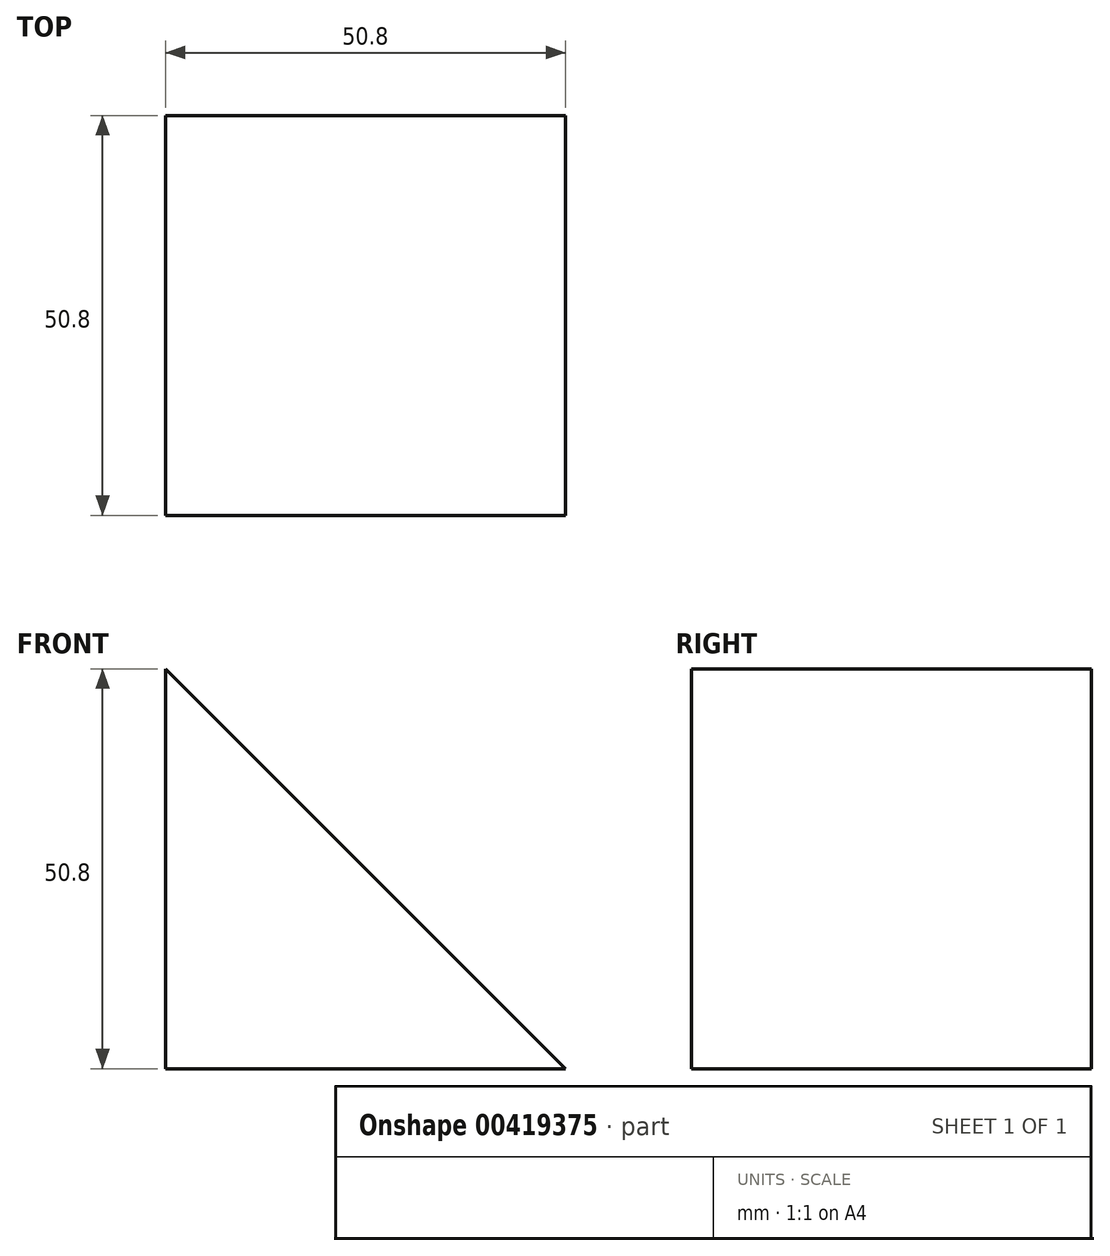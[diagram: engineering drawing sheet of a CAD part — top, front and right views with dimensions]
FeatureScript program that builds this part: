
annotation { "Feature Type Name" : "Feature", "Feature Type Description" : "" }
export const myFeature = defineFeature(function(context is Context, id is Id, definition is map)
    precondition{}
    {
        {
            var Q0;
            Q0=qCreatedBy(makeId("Front.planeOp"),FACE);
            var sketch = newSketch(context, id + "F0", { "sketchPlane" : qUnion([Q0])});
            skLineSegment(sketch, "E0", {"start": v(0, 0) * mm, "end": v(50.8, 0) * mm});
            skLineSegment(sketch, "E1", {"start": v(0, 0) * mm, "end": v(0, 50.8) * mm});
            skLineSegment(sketch, "E2", {"start": v(0, 50.8) * mm, "end": v(50.8, 0) * mm});
            skSolve(sketch);
        }
        {
            var Q0;
            Q0 = qSketchRegion(id + "F0", true);
            extrude(context, id + "F1", {"entities" : qUnion([Q0]), "depth" : 50.8 * mm});
        }
    });
